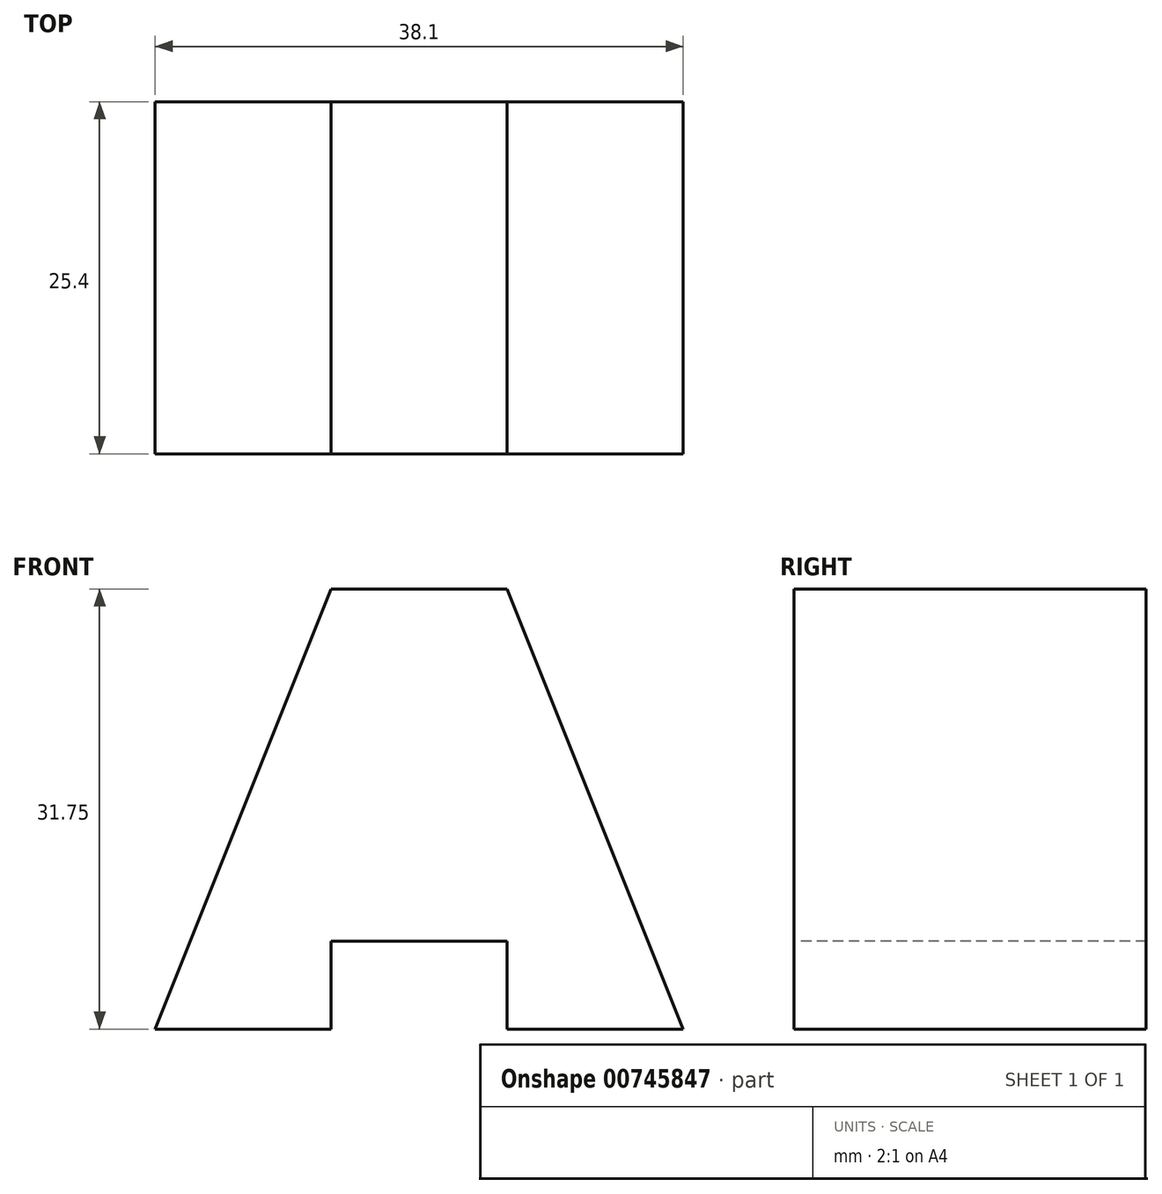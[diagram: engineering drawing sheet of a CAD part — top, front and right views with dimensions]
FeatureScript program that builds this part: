
annotation { "Feature Type Name" : "Feature", "Feature Type Description" : "" }
export const myFeature = defineFeature(function(context is Context, id is Id, definition is map)
    precondition{}
    {
        {
            var Q0;
            Q0=qCreatedBy(makeId("Front.planeOp"),FACE);
            var sketch = newSketch(context, id + "F0", { "sketchPlane" : qUnion([Q0])});
            skLineSegment(sketch, "E0", {"start": v(0, 0) * mm, "end": v(38.1, 0) * mm});
            skLineSegment(sketch, "E1", {"start": v(38.1, 0) * mm, "end": v(38.1, 31.75) * mm});
            skLineSegment(sketch, "E2", {"start": v(38.1, 31.75) * mm, "end": v(0, 31.75) * mm});
            skLineSegment(sketch, "E3", {"start": v(0, 31.75) * mm, "end": v(0, 0) * mm});
            skSolve(sketch);
        }
        {
            var Q0;
            Q0 = qSketchRegion(id + "F0", true);
            extrude(context, id + "F1", {"entities" : qUnion([Q0]), "depth" : 25.4 * mm, "offsetDistance" : 25.4 * mm});
        }
        {
            var Q0;
            Q0=makeQuery(id+"F1.opExtrude","CAP_FACE",FACE,{"disambiguationData":[OSD([sQuery(id+"F0.wireOp",EDGE,"E0"),sQuery(id+"F0.wireOp",EDGE,"E1"),sQuery(id+"F0.wireOp",EDGE,"E2"),sQuery(id+"F0.wireOp",EDGE,"E3")])],"isStart":false});
            var sketch = newSketch(context, id + "F2", { "sketchPlane" : qUnion([Q0])});
            skLineSegment(sketch, "E4", {"start": v(12.7, 0) * mm, "end": v(12.7, 6.35) * mm});
            skLineSegment(sketch, "E5", {"start": v(12.7, 6.35) * mm, "end": v(25.4, 6.35) * mm});
            skLineSegment(sketch, "E6", {"start": v(25.4, 6.35) * mm, "end": v(25.4, 0) * mm});
            skSolve(sketch);
        }
        {
            var Q0;
            {var subQ0=sQuery(id+"F2.wireOp",EDGE,"E4");Q0=makeQuery(id+"F2.imprint","IMPRINT",FACE,{"disambiguationData":[TD([[makeQuery(id+"F2.imprint","IMPRINT",EDGE,{"derivedFrom":subQ0}),-1.0]])]});}
            extrude(context, id + "F3", {"entities" : qUnion([Q0]), "operationType" : NewBodyOperationType.REMOVE, "endBound" : BoundingType.THROUGH_ALL, "oppositeDirection" : true, "depth" : 25.4 * mm, "offsetDistance" : 25.4 * mm});
        }
        {
            var Q0;
            Q0=makeQuery(id+"F1.opExtrude","CAP_FACE",FACE,{"disambiguationData":[OSD([sQuery(id+"F0.wireOp",EDGE,"E0"),sQuery(id+"F0.wireOp",EDGE,"E1"),sQuery(id+"F0.wireOp",EDGE,"E2"),sQuery(id+"F0.wireOp",EDGE,"E3")])],"isStart":false});
            var sketch = newSketch(context, id + "F4", { "sketchPlane" : qUnion([Q0])});
            skLineSegment(sketch, "E7", {"start": v(38.1, 0) * mm, "end": v(25.4, 31.75) * mm});
            skLineSegment(sketch, "E8", {"start": v(0, 0) * mm, "end": v(12.7, 31.75) * mm});
            skSolve(sketch);
        }
        {
            var Q0;
            {var subQ0=sQuery(id+"F4.wireOp",EDGE,"E8");Q0=makeQuery(id+"F4.imprint","IMPRINT",FACE,{"disambiguationData":[TD([[makeQuery(id+"F4.imprint","IMPRINT",EDGE,{"derivedFrom":subQ0}),1.0]])]});}
            var Q1;
            {var subQ0=sQuery(id+"F4.wireOp",EDGE,"E7");Q1=makeQuery(id+"F4.imprint","IMPRINT",FACE,{"disambiguationData":[TD([[makeQuery(id+"F4.imprint","IMPRINT",EDGE,{"derivedFrom":subQ0}),-1.0]])]});}
            extrude(context, id + "F5", {"entities" : qUnion([Q0, Q1]), "operationType" : NewBodyOperationType.REMOVE, "endBound" : BoundingType.THROUGH_ALL, "oppositeDirection" : true, "depth" : 25.4 * mm, "offsetDistance" : 25.4 * mm});
        }
    });
